# Revit family: PRD_AR_MltFnctnDspnsrs_STRATOSPaperTowelWasteBinCombination_STR602E
name_source: partatom
category: Specialty Equipment
units: mm (PartAtom-declared; Revit-internal decimal feet)

## family parameters
Cut with Voids When Loaded = Yes
Host = Face
OmniClass Number = 23.40.20.21.17
OmniClass Title = Paper Towel Dispensers, Disposal Units
Part Type = Normal
Room Calculation Point = No
Round Connector Dimension = Use Diameter
Shared = No

## types (1)
- STR602E
    AssetType = Fixed
    BIMObjectName = PRD_AR_MultiFunctionDispensers_STRATOSPaperTowelWasteBinCombination_STR602E
    Category = Pr_40_70_22_52, Multi-function dispensers
    CombinationPart1 = Paper towel dispenser
    CombinationPart2 = Waste bin
    Default Elevation = 850 mm  [stored 2.78871 ft]
    Description = STRATOS paper towel dispenser and waste bin combination for recessed mounting, stainless steel, surface satin finished, material thickness 1.5 mm, curved front with inspection window, both parts with cylinder lock and key, paper towel dispenser capacity 300-400 pieces for paper with Z-fold, waste bin with approx. 22 litre capacity, integrated bag holder, including mounting material.
    DispenserMaterial = PRD_AR_StainlessSteel_SatinFinished
    DurationUnit = year
    Features = stainless steel, surface satin finished
    FillingQuantity1 = 400
    FillingQuantity1Uom = Pieces
    FillingQuantity2 = 22
    FillingQuantity2Uom = Liter
    Finish = satin finished
    GrossWeight = 18.22 kg
    IfcExportAs = IfcFurnitureType
    IfcExportType = USERDEFINED
    IntegralAccessories = incl. stainless steel screws and dowels
    IsBuiltIn = TRUE
    Lock1 = Key-lock
    Lock2 = Key-lock
    MainColor = stainless steel
    Manufacturer = KWC Group Management AG
    ManufacturerName = KWC Group Management AG
    ManufacturerURL = www.kwc-professional.com
    Material = stainless steel
    MaterialCode = 1.4301
    MaterialThickness = 1.50 mm
    Model = STR602E
    ModelNumber = 3600008932
    ModelReference = STR602E
    NBSDescription = Multi-function dispensers
    NBSReference = 45-35-72/384
    Name = STRATOS Paper Towel Waste Bin Combination STR602E
    NetWeight = 15.65 kg
    NominalDepth = 203 mm  [stored 0.66601 ft]
    NominalHeight = 1162 mm  [stored 3.81234 ft]
    NominalWidth = 328 mm  [stored 1.07612 ft]
    Offset = 0 mm  [stored 0 ft]
    ProductInformation = http://pim.kwc.com
    Size = 328 x 1162 x 203 mm
    TypeOfConsumable1 = Paper towel
    TypeOfFixing = Screw
    TypeOfMounting = Recessed mounting
    URL = www.kwc-professional.com
    Uniclass2015Code = Pr_40_70_22_52
    Uniclass2015Title = Multi-function dispensers
    Uniclass2015Version = Products v1.10
    Version = 1
    WarrantyDurationUnit = year

note: [stored X ft] marks values corroborated as IEEE doubles in the binary element streams (Revit-internal decimal feet)

## geometry (parser evidence)
native form markers: Sweep x4
no freeform markers — native parametric forms only
